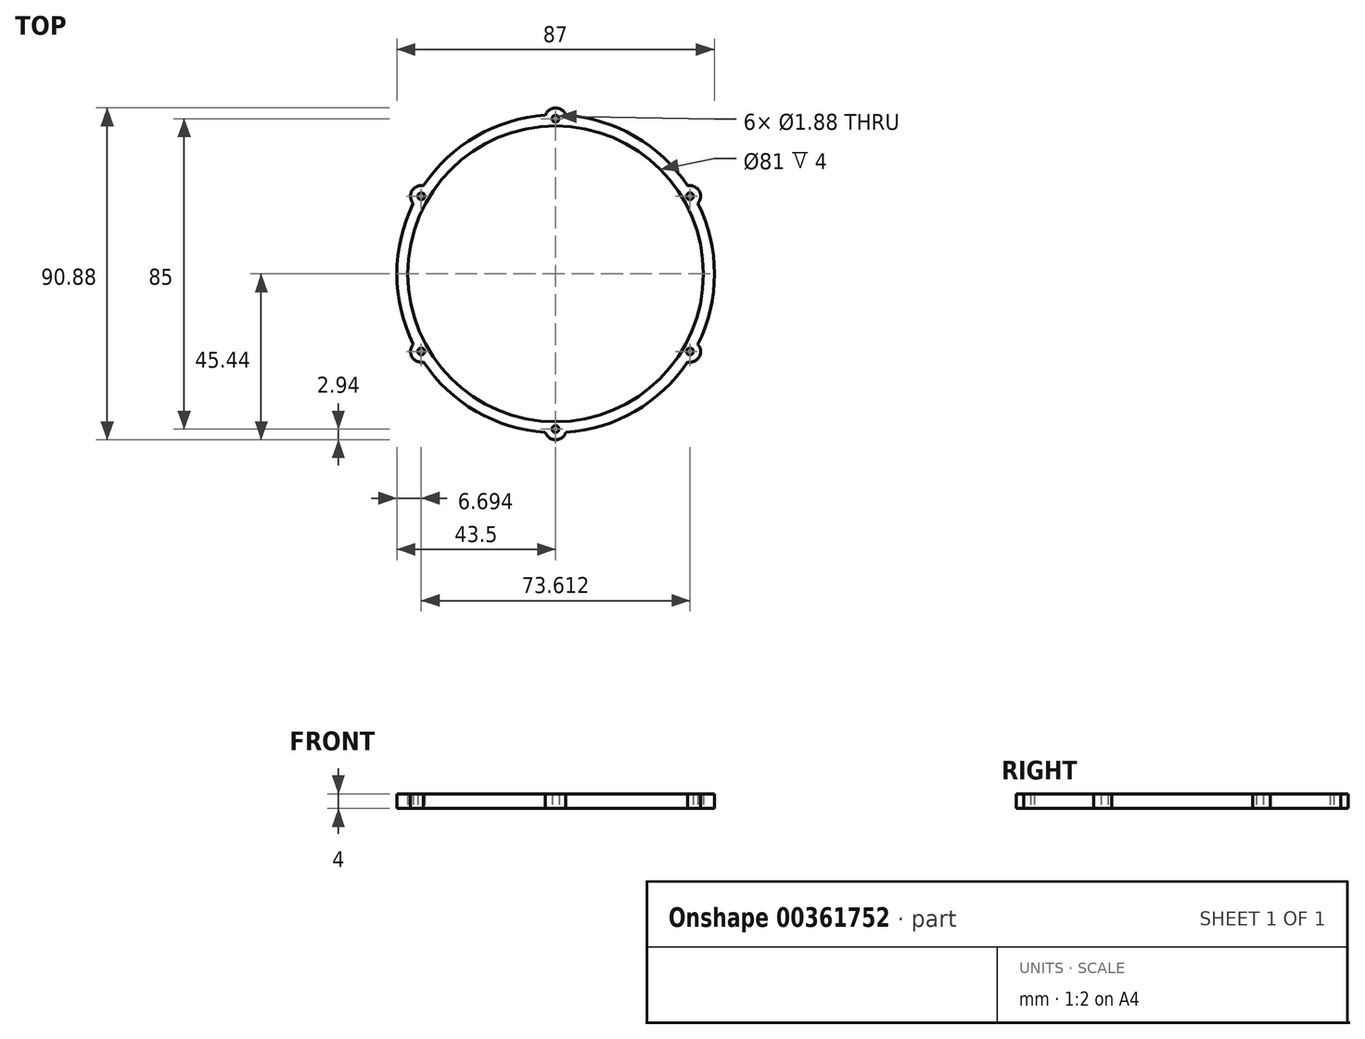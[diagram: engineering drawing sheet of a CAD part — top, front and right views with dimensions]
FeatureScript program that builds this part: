
annotation { "Feature Type Name" : "Feature", "Feature Type Description" : "" }
export const myFeature = defineFeature(function(context is Context, id is Id, definition is map)
    precondition{}
    {
        {
            var Q0;
            Q0=qCreatedBy(makeId("Top.planeOp"),FACE);
            var sketch = newSketch(context, id + "F0", { "sketchPlane" : qUnion([Q0])});
            skCircle(sketch, "E0", {"center": v(0, 0) * mm, "radius": 40.5 * mm});
            skArc(sketch, "E1", {"start": v(-2.8, 43.4) * mm, "mid": v(-21.75, 37.67) * mm, "end": v(-36.2, 24.13) * mm});
            skCircle(sketch, "E2", {"center": v(0, 42.5) * mm, "radius": 0.94 * mm});
            skArc(sketch, "E3.0", {"start": v(2.8, 43.4) * mm, "mid": v(0, 45.44) * mm, "end": v(-2.8, 43.4) * mm});
            skArc(sketch, "E4.1.0", {"start": v(-36.2, 24.13) * mm, "mid": v(-39.35, 22.72) * mm, "end": v(-39, 19.28) * mm});
            skCircle(sketch, "E4.1.1", {"center": v(-36.8, 21.25) * mm, "radius": 0.94 * mm});
            skArc(sketch, "E4.2.0", {"start": v(-39, -19.28) * mm, "mid": v(-39.35, -22.72) * mm, "end": v(-36.2, -24.13) * mm});
            skCircle(sketch, "E4.2.1", {"center": v(-36.8, -21.25) * mm, "radius": 0.94 * mm});
            skArc(sketch, "E4.3.0", {"start": v(-2.8, -43.4) * mm, "mid": v(0, -45.44) * mm, "end": v(2.8, -43.4) * mm});
            skCircle(sketch, "E4.3.1", {"center": v(0, -42.5) * mm, "radius": 0.94 * mm});
            skArc(sketch, "E4.4.0", {"start": v(36.2, -24.13) * mm, "mid": v(39.35, -22.72) * mm, "end": v(39, -19.28) * mm});
            skCircle(sketch, "E4.4.1", {"center": v(36.8, -21.25) * mm, "radius": 0.94 * mm});
            skArc(sketch, "E4.5.0", {"start": v(39, 19.28) * mm, "mid": v(39.35, 22.72) * mm, "end": v(36.2, 24.13) * mm});
            skCircle(sketch, "E4.5.1", {"center": v(36.8, 21.25) * mm, "radius": 0.94 * mm});
            skArc(sketch, "E5.trimOffspring", {"start": v(-39, 19.28) * mm, "mid": v(-43.5, 0) * mm, "end": v(-39, -19.28) * mm});
            skArc(sketch, "E6.trimOffspring", {"start": v(-36.2, -24.13) * mm, "mid": v(-21.75, -37.67) * mm, "end": v(-2.8, -43.4) * mm});
            skArc(sketch, "E7.trimOffspring", {"start": v(39, -19.28) * mm, "mid": v(43.5, 0) * mm, "end": v(39, 19.28) * mm});
            skArc(sketch, "E8.trimOffspring", {"start": v(36.2, 24.13) * mm, "mid": v(21.75, 37.67) * mm, "end": v(2.8, 43.4) * mm});
            skArc(sketch, "E9.trimOffspring", {"start": v(2.8, -43.4) * mm, "mid": v(21.75, -37.67) * mm, "end": v(36.2, -24.13) * mm});
            skSolve(sketch);
        }
        {
            var Q0;
            Q0=makeQuery(id+"F0.imprint","IMPRINT",FACE,{"disambiguationData":[TD([[makeQuery(id+"F0.imprint","IMPRINT",EDGE,{"derivedFrom":sQuery(id+"F0.wireOp",EDGE,"E0")}),-1.0]])]});
            extrude(context, id + "F1", {"entities" : qUnion([Q0]), "depth" : 4 * mm, "offsetDistance" : 25 * mm});
        }
    });
